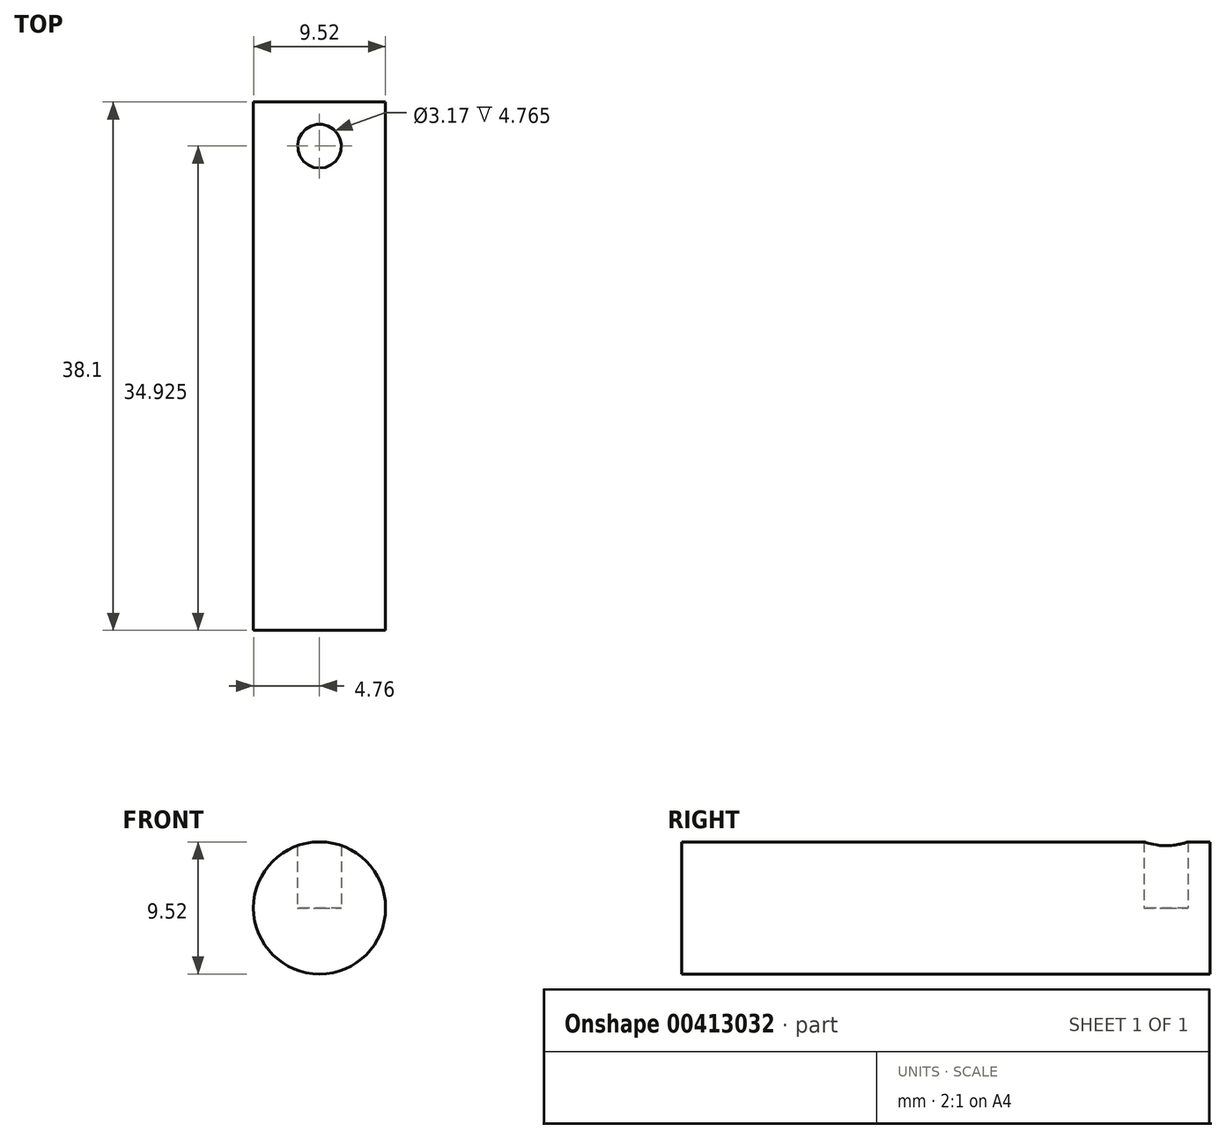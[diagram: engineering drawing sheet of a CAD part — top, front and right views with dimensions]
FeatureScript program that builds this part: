
annotation { "Feature Type Name" : "Feature", "Feature Type Description" : "" }
export const myFeature = defineFeature(function(context is Context, id is Id, definition is map)
    precondition{}
    {
        {
            var Q0;
            Q0=qCreatedBy(makeId("Front.planeOp"),FACE);
            var sketch = newSketch(context, id + "F0", { "sketchPlane" : qUnion([Q0])});
            skCircle(sketch, "E0", {"center": v(0, 0) * mm, "radius": 4.76 * mm});
            skSolve(sketch);
        }
        {
            var Q0;
            Q0=makeQuery(id+"F0.imprint","IMPRINT",FACE,{"disambiguationData":[TD([[makeQuery(id+"F0.imprint","IMPRINT",EDGE,{"derivedFrom":sQuery(id+"F0.wireOp",EDGE,"E0")}),1.0]])]});
            extrude(context, id + "F1", {"entities" : qUnion([Q0]), "depth" : 38.1 * mm});
        }
        {
            var Q0;
            Q0=qCreatedBy(makeId("Top.planeOp"),FACE);
            var sketch = newSketch(context, id + "F2", { "sketchPlane" : qUnion([Q0])});
            skCircle(sketch, "E1", {"center": v(0, -3.18) * mm, "radius": 1.59 * mm});
            skSolve(sketch);
        }
        {
            var Q0;
            Q0 = qSketchRegion(id + "F2", true);
            extrude(context, id + "F3", {"entities" : qUnion([Q0]), "operationType" : NewBodyOperationType.REMOVE, "depth" : 25.4 * mm});
        }
    });
